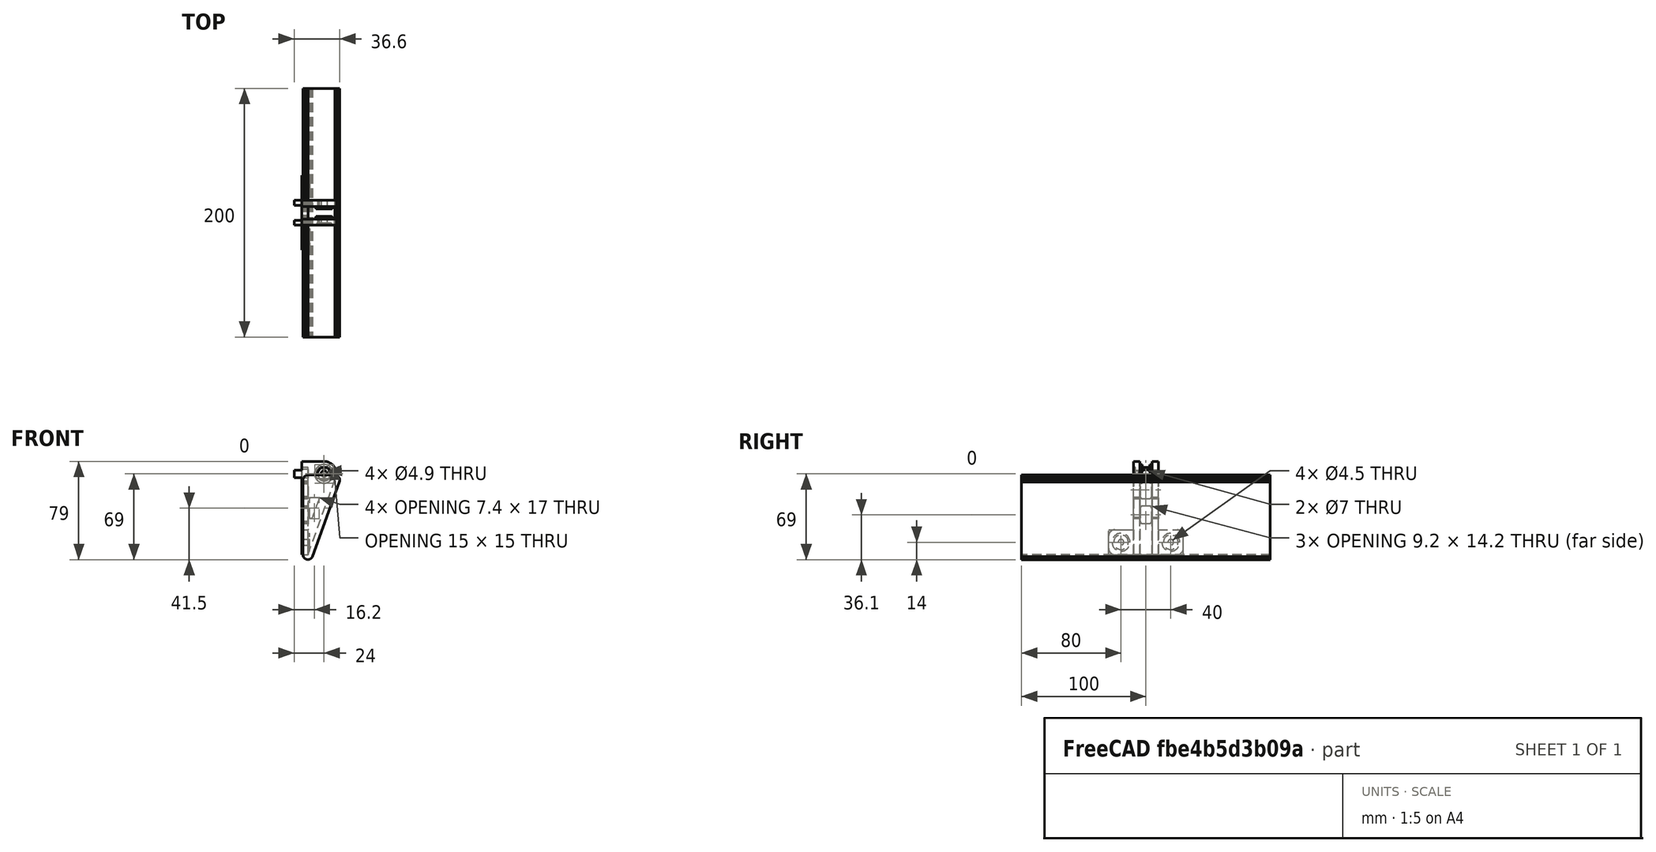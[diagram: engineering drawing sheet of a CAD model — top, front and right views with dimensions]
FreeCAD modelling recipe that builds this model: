
FCSTD DOCUMENT  (FreeCAD 0.19R24267 +99 (Git))
Label: ApoyoFrontalV0
License: All rights reserved
LicenseURL: http://en.wikipedia.org/wiki/All_rights_reserved
objects: Part::Feature×39, Part::Box×13, Part::Cylinder×13, Part::Fuse×10, Part::MultiFuse×6, Part::FeaturePython×6, Part::Chamfer×6, Part::Cut×5, Part::Fillet×4, Part::Extrusion×3, Part::Prism×1, Part::Mirroring×1, Part::Part2DObjectPython×1, App::DocumentObjectGroupPython×1, Part::Refine×1
note: 109 computed .brp shape members not serialized (recipe doc carries the construction recipe); baked Part::Feature solids carry a one-line shape summary decoded from their .brp

FEATURE [Part::Box] cube
  AttacherType = Attacher::AttachEngine3D
  Height = 5
  Length = 20
  Placement = pos=(-10,-10,0) rot=(0,0,1;0rad)
  Width = 20
FEATURE [Part::Cylinder] cylinder
  Angle = 360
  AttacherType = Attacher::AttachEngine3D
  Height = 100
  Placement = pos=(0,0,-50) rot=(0,0,1;0rad)
  Radius = 3.5
FEATURE [Part::Cut] difference
  Base = -> cube
  Tool = -> cylinder
FEATURE [Part::Box] cube001
  AttacherType = Attacher::AttachEngine3D
  Height = 11
  Length = 4
  Placement = pos=(6,-3,0) rot=(0,0,1;0rad)
  Width = 6
FEATURE [Part::Box] cube002
  AttacherType = Attacher::AttachEngine3D
  Height = 11
  Length = 4
  Placement = pos=(3,6,0) rot=(0,0,1;1.5708rad)
  Width = 6
FEATURE [Part::Box] cube003
  AttacherType = Attacher::AttachEngine3D
  Height = 11
  Length = 4
  Placement = pos=(-6,3,0) rot=(0,0,1;3.14159rad)
  Width = 6
FEATURE [Part::Box] cube004
  AttacherType = Attacher::AttachEngine3D
  Height = 11
  Length = 4
  Placement = pos=(-3,-6,0) rot=(0,0,-1;1.5708rad)
  Width = 6
FEATURE [Part::MultiFuse] Group
  Shapes = -> [cube001,cube002,cube003,cube004]
FEATURE [Part::Fuse] Group001
  Base = -> difference
  Tool = -> Group
FEATURE [Part::Box] cube005
  AttacherType = Attacher::AttachEngine3D
  Height = 100
  Length = 100
  Placement = pos=(5.15,-5,-50) rot=(0,0,1;0rad)
  Width = 10
FEATURE [Part::Box] cube006
  AttacherType = Attacher::AttachEngine3D
  Height = 100
  Length = 100
  Placement = pos=(5.15,-5,-50) rot=(0,0,1;0rad)
  Width = 10
FEATURE [Part::Fuse] Group002
  Base = -> cube005
  Tool = -> cube006
FEATURE [Part::Cut] difference001
  Base = -> Group001
  Tool = -> Group002
FEATURE [Part::Box] cube007
  AttacherType = Attacher::AttachEngine3D
  Height = 13
  Length = 20
  Placement = pos=(-10,-10,-13) rot=(0,0,1;0rad)
  Width = 5
FEATURE [Part::Cylinder] cylinder001
  Angle = 360
  AttacherType = Attacher::AttachEngine3D
  Height = 5
  Placement = pos=(0,10,-13) rot=(1,0,0;1.5708rad)
  Radius = 10
FEATURE [Part::Cylinder] cylinder002
  Angle = 360
  AttacherType = Attacher::AttachEngine3D
  Height = 7
  Placement = pos=(0,10,-13) rot=(1,0,0;1.5708rad)
  Radius = 7.5
FEATURE [Part::MultiFuse] union
  Shapes = -> [cube007,cylinder001,cylinder002]
FEATURE [Part::Box] cube008
  AttacherType = Attacher::AttachEngine3D
  Height = 13
  Length = 20
  Placement = pos=(-10,-10,-13) rot=(0,0,1;0rad)
  Width = 5
FEATURE [Part::Cylinder] cylinder003
  Angle = 360
  AttacherType = Attacher::AttachEngine3D
  Height = 5
  Placement = pos=(0,10,-13) rot=(1,0,0;1.5708rad)
  Radius = 10
FEATURE [Part::Cylinder] cylinder004
  Angle = 360
  AttacherType = Attacher::AttachEngine3D
  Height = 7
  Placement = pos=(0,10,-13) rot=(1,0,0;1.5708rad)
  Radius = 7.5
FEATURE [Part::MultiFuse] union001
  Placement = pos=(0,0,0) rot=(0,0,1;3.14159rad)
  Shapes = -> [cube008,cylinder003,cylinder004]
FEATURE [Part::Fuse] Group003
  Base = -> union
  Tool = -> union001
FEATURE [Part::Cylinder] cylinder005
  Angle = 360
  AttacherType = Attacher::AttachEngine3D
  Height = 1000
  Placement = pos=(0,0,-500) rot=(0,0,1;0rad)
  Radius = 5
FEATURE [Part::Cylinder] cylinder006
  Angle = 360
  AttacherType = Attacher::AttachEngine3D
  Height = 1000
  Placement = pos=(0,500,-13) rot=(1,0,0;1.5708rad)
  Radius = 2.45
FEATURE [Part::Prism] prism
  AttacherType = Attacher::AttachEngine3D
  Circumradius = 5.79
  FirstAngle = 0
  Height = 5
  Placement = pos=(0,-8.33333,-13) rot=(0.57735,0.57735,-0.57735;2.0944rad)
  Polygon = 6
  SecondAngle = 0
FEATURE [Part::MultiFuse] union002
  Shapes = -> [cylinder005,cylinder006,prism]
FEATURE [Part::Cut] difference002
  Base = -> Group003
  Tool = -> union002
FEATURE [Part::Fuse] Group004
  Base = -> difference001
  Placement = pos=(0,0,45) rot=(0,-1,0;1.5708rad)
  Tool = -> difference002
FEATURE [Part::Box] cube009
  AttacherType = Attacher::AttachEngine3D
  Height = 20
  Length = 5
  Placement = pos=(-5,-30,-20) rot=(0,0,1;0rad)
  Width = 60
FEATURE [Part::Cylinder] cylinder007
  Angle = 360
  AttacherType = Attacher::AttachEngine3D
  Height = 6.5
  Radius = 7.25
FEATURE [Part::Cylinder] cylinder008
  Angle = 360
  AttacherType = Attacher::AttachEngine3D
  Height = 6.5
  Placement = pos=(0,40,0) rot=(0,0,1;0rad)
  Radius = 7.25
FEATURE [Part::Fuse] Group005
  Base = -> cylinder007
  Placement = pos=(-5,-20,-10) rot=(0,1,0;1.5708rad)
  Tool = -> cylinder008
FEATURE [Part::Box] cube010
  AttacherType = Attacher::AttachEngine3D
  Height = 35
  Length = 5
  Placement = pos=(-5,-10,0) rot=(0,0,1;0rad)
  Width = 20
FEATURE [Part::MultiFuse] union003
  Shapes = -> [Group004,cube009,Group005,cube010]
FEATURE [Part::Cylinder] cylinder009
  Angle = 360
  AttacherType = Attacher::AttachEngine3D
  Height = 15
  Placement = pos=(0,0,-7.5) rot=(0,0,1;0rad)
  Radius = 2.25
FEATURE [Part::Cylinder] cylinder010
  Angle = 360
  AttacherType = Attacher::AttachEngine3D
  Height = 15
  Placement = pos=(0,40,-7.5) rot=(0,0,1;0rad)
  Radius = 2.25
FEATURE [Part::Fuse] Group006
  Base = -> cylinder009
  Placement = pos=(-5,-20,-10) rot=(0,1,0;1.5708rad)
  Tool = -> cylinder010
FEATURE [Part::Box] cube011
  AttacherType = Attacher::AttachEngine3D
  Height = 10
  Length = 20
  Width = 5
FEATURE [Part::Cylinder] cylinder011
  Angle = 360
  AttacherType = Attacher::AttachEngine3D
  Height = 0.01
  Placement = pos=(-0.005,0,0) rot=(0.57735,0.57735,0.57735;2.0944rad)
  Radius = 2.1
FEATURE [Part::FeaturePython] minkowski  # WARN: FeaturePython — macro-defined, semantics opaque (R4)
  Arguments = {'convexity': '0'}
  Children = -> [cube011,cylinder011]
  Operation = minkowski
FEATURE [Part::Box] cube012
  AttacherType = Attacher::AttachEngine3D
  Height = 10
  Length = 20
  Width = 5
FEATURE [Part::Cylinder] cylinder012
  Angle = 360
  AttacherType = Attacher::AttachEngine3D
  Height = 0.01
  Placement = pos=(-0.005,0,0) rot=(0.57735,0.57735,0.57735;2.0944rad)
  Radius = 2.1
FEATURE [Part::FeaturePython] minkowski001  # WARN: FeaturePython — macro-defined, semantics opaque (R4)
  Arguments = {'convexity': '0'}
  Children = -> [cube012,cylinder012]
  Operation = minkowski
  Placement = pos=(0,0,20) rot=(0,0,1;0rad)
FEATURE [Part::Fuse] Group007
  Base = -> minkowski
  Placement = pos=(-20,-2.5,7.1) rot=(0,0,1;0rad)
  Tool = -> minkowski001
FEATURE [Part::Fuse] union004
  Base = -> Group006
  Tool = -> Group007
FEATURE [Part::Cut] difference003
  Base = -> union003
  Tool = -> union004
FEATURE [Part::Feature] polygon
  shape: bbox 60 x 21.6 x 2e-07 mm, 1 faces, 0 solids (baked)
FEATURE [Part::FeaturePython] RefineLinearExtrude  # WARN: FeaturePython — macro-defined, semantics opaque (R4)
  Base = -> polygon
FEATURE [Part::Extrusion] LinearExtrude
  Base = -> RefineLinearExtrude
  Dir = (0,0,5)
  DirMode = 0
  FaceMakerClass = Part::FaceMakerBullseye
  LengthFwd = 0
  LengthRev = 0
  Placement = pos=(0,10,40) rot=(0.57735,0.57735,-0.57735;2.0944rad)
  Solid = false
  Symmetric = false
FEATURE [Part::Feature] polygon001
  shape: bbox 60 x 21.6 x 2e-07 mm, 1 faces, 0 solids (baked)
FEATURE [Part::FeaturePython] RefineLinearExtrude001  # WARN: FeaturePython — macro-defined, semantics opaque (R4)
  Base = -> polygon001
FEATURE [Part::Extrusion] LinearExtrude001
  Base = -> RefineLinearExtrude001
  Dir = (0,0,5)
  DirMode = 0
  FaceMakerClass = Part::FaceMakerBullseye
  LengthFwd = 0
  LengthRev = 0
  Placement = pos=(0,10,40) rot=(0.57735,0.57735,-0.57735;2.0944rad)
  Solid = false
  Symmetric = false
FEATURE [Part::Mirroring] mirr_LinearExtrude001  label="mirrored LinearExtrude001"
  Base = (0,0,0)
  Normal = (0,1,0)
  Source = -> LinearExtrude001
FEATURE [Part::Fuse] union005
  Base = -> LinearExtrude
  Tool = -> mirr_LinearExtrude001
FEATURE [Part::Feature] polygon002
  shape: bbox 60 x 21.6 x 2e-07 mm, 1 faces, 0 solids (baked)
FEATURE [Part::Part2DObjectPython] circle  # Draft 2D object (typed FeaturePython)
  Area = 50.2655
  FirstAngle = 0
  LastAngle = 0
  MakeFace = true
  Radius = 4
FEATURE [Part::FeaturePython] minkowski002  # WARN: FeaturePython — macro-defined, semantics opaque (R4)
  Arguments = {'convexity': '0'}
  Children = -> [polygon002,circle]
  Operation = minkowski
FEATURE [Part::FeaturePython] RefineLinearExtrude002  # WARN: FeaturePython — macro-defined, semantics opaque (R4)
  Base = -> minkowski002
FEATURE [Part::Extrusion] LinearExtrude002
  Base = -> RefineLinearExtrude002
  Dir = (0,0,200)
  DirMode = 0
  FaceMakerClass = Part::FaceMakerBullseye
  LengthFwd = 0
  LengthRev = 0
  Placement = pos=(0,100,40) rot=(0.57735,0.57735,-0.57735;2.0944rad)
  Solid = false
  Symmetric = false
FEATURE [App::DocumentObjectGroupPython] LayerContainer  label="Capas"  # scripted group (container) (typed FeaturePython)
FEATURE [Part::Feature] Line
  shape: bbox 0.2275 x 0.75 x 2e-07 mm, 0 faces, 0 solids (baked)
FEATURE [Part::Feature] Line001
  shape: bbox 0.3691 x 0.6924 x 2e-07 mm, 0 faces, 0 solids (baked)
FEATURE [Part::Feature] Line002
  shape: bbox 0.4981 x 0.6055 x 2e-07 mm, 0 faces, 0 solids (baked)
FEATURE [Part::Feature] Line003
  shape: bbox 0.6055 x 0.4981 x 2e-07 mm, 0 faces, 0 solids (baked)
FEATURE [Part::Feature] Line004
  shape: bbox 0.6924 x 0.3691 x 2e-07 mm, 0 faces, 0 solids (baked)
FEATURE [Part::Feature] Line005
  shape: bbox 0.75 x 0.2275 x 2e-07 mm, 0 faces, 0 solids (baked)
FEATURE [Part::Feature] Line006
  shape: bbox 0.7803 x 0.07715 x 2e-07 mm, 0 faces, 0 solids (baked)
FEATURE [Part::Feature] Line007
  shape: bbox 60 x 2e-07 x 2e-07 mm, 0 faces, 0 solids (baked)
FEATURE [Part::Feature] Line008
  shape: bbox 0.7803 x 0.07715 x 2e-07 mm, 0 faces, 0 solids (baked)
FEATURE [Part::Feature] Line009
  shape: bbox 0.75 x 0.2275 x 2e-07 mm, 0 faces, 0 solids (baked)
FEATURE [Part::Feature] Line010
  shape: bbox 0.6924 x 0.3691 x 2e-07 mm, 0 faces, 0 solids (baked)
FEATURE [Part::Feature] Line011
  shape: bbox 0.6054 x 0.4981 x 2e-07 mm, 0 faces, 0 solids (baked)
FEATURE [Part::Feature] Line012
  shape: bbox 0.4981 x 0.6055 x 2e-07 mm, 0 faces, 0 solids (baked)
FEATURE [Part::Feature] Line013
  shape: bbox 0.3691 x 0.6924 x 2e-07 mm, 0 faces, 0 solids (baked)
FEATURE [Part::Feature] Line014
  shape: bbox 0.2276 x 0.75 x 2e-07 mm, 0 faces, 0 solids (baked)
FEATURE [Part::Feature] Line015
  shape: bbox 0.0771 x 0.7803 x 2e-07 mm, 0 faces, 0 solids (baked)
FEATURE [Part::Feature] Line016
  shape: bbox 0.0771 x 0.7803 x 2e-07 mm, 0 faces, 0 solids (baked)
FEATURE [Part::Feature] Line017
  shape: bbox 0.2276 x 0.75 x 2e-07 mm, 0 faces, 0 solids (baked)
FEATURE [Part::Feature] Line018
  shape: bbox 0.3691 x 0.6924 x 2e-07 mm, 0 faces, 0 solids (baked)
FEATURE [Part::Feature] Line019
  shape: bbox 0.4981 x 0.6055 x 2e-07 mm, 0 faces, 0 solids (baked)
FEATURE [Part::Feature] Line020
  shape: bbox 0.6054 x 0.4981 x 2e-07 mm, 0 faces, 0 solids (baked)
FEATURE [Part::Feature] Line021
  shape: bbox 0.6924 x 0.3691 x 2e-07 mm, 0 faces, 0 solids (baked)
FEATURE [Part::Feature] Line022
  shape: bbox 60 x 21.6 x 2e-07 mm, 0 faces, 0 solids (baked)
FEATURE [Part::Feature] Line023
  shape: bbox 0.75 x 0.2276 x 2e-07 mm, 0 faces, 0 solids (baked)
FEATURE [Part::Feature] Line024
  shape: bbox 0.7803 x 0.0771 x 2e-07 mm, 0 faces, 0 solids (baked)
FEATURE [Part::Feature] Line025
  shape: bbox 0.7803 x 0.0771 x 2e-07 mm, 0 faces, 0 solids (baked)
FEATURE [Part::Feature] Line026
  shape: bbox 0.75 x 0.2276 x 2e-07 mm, 0 faces, 0 solids (baked)
FEATURE [Part::Feature] Line027
  shape: bbox 0.6924 x 0.3691 x 2e-07 mm, 0 faces, 0 solids (baked)
FEATURE [Part::Feature] Line028
  shape: bbox 0.6055 x 0.4981 x 2e-07 mm, 0 faces, 0 solids (baked)
FEATURE [Part::Feature] Line029
  shape: bbox 0.4981 x 0.6054 x 2e-07 mm, 0 faces, 0 solids (baked)
FEATURE [Part::Feature] Line030
  shape: bbox 0.3691 x 0.6924 x 2e-07 mm, 0 faces, 0 solids (baked)
FEATURE [Part::Feature] Line031
  shape: bbox 0.2275 x 0.75 x 2e-07 mm, 0 faces, 0 solids (baked)
FEATURE [Part::Feature] Line032
  shape: bbox 0.07715 x 0.7803 x 2e-07 mm, 0 faces, 0 solids (baked)
FEATURE [Part::Feature] Line033
  shape: bbox 2e-07 x 21.6 x 2e-07 mm, 0 faces, 0 solids (baked)
FEATURE [Part::Feature] Line034
  shape: bbox 0.07715 x 0.7803 x 2e-07 mm, 0 faces, 0 solids (baked)
FEATURE [Part::Feature] Matrix_Deformation
  Placement = pos=(2.5,100,55) rot=(0.57735,0.57735,-0.57735;2.0944rad)
  shape: bbox 7.4 x 200 x 17 mm, 37 faces (baked)
FEATURE [Part::Cut] difference004
  Base = -> union005
  Tool = -> Matrix_Deformation
FEATURE [Part::Fuse] Group008
  Base = -> difference003
  Tool = -> difference004
FEATURE [Part::MultiFuse] Fusion
  Shapes = -> [difference003,difference004]
FEATURE [Part::Refine] Fusion001
  Source = -> Fusion
FEATURE [Part::Chamfer] Chamfer
  Base = -> Fusion001
  Edges = 1 edges r=1.4: [Edge32]
FEATURE [Part::Chamfer] Chamfer001
  Base = -> Chamfer
  Edges = 1 edges r=1.4: [Edge1069]
FEATURE [Part::Fillet] Fillet
  Base = -> Chamfer001
  Edges = 1 edges r=5: [Edge426]
FEATURE [Part::Fillet] Fillet001
  Base = -> Fillet
  Edges = 1 edges r=5: [Edge282]
FEATURE [Part::Fillet] Fillet002
  Base = -> Fillet001
  Edges = 1 edges r=5: [Edge298]
FEATURE [Part::Fillet] Fillet003
  Base = -> Fillet002
  Edges = 1 edges r=5: [Edge333]
FEATURE [Part::Chamfer] Chamfer002
  Base = -> Fillet003
  Edges = 1 edges r=1.9: [Edge1117]
FEATURE [Part::Chamfer] Chamfer003
  Base = -> Chamfer002
  Edges = 1 edges r=1.9: [Edge63]
FEATURE [Part::Chamfer] Chamfer004
  Base = -> Chamfer003
  Edges = 1 edges r=1.9: [Edge1136]
FEATURE [Part::Chamfer] Chamfer005
  Base = -> Chamfer004
  Edges = 1 edges r=1.9: [Edge61]
